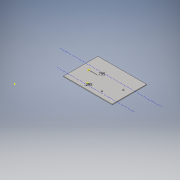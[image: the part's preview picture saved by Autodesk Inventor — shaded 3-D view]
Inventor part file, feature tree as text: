
AUTODESK INVENTOR PART (.ipt)
format: ipt  version: 2016 (Build 200138000, 138)  size: 113,664 bytes
history: native  units: in
note: dims shown in document units (in); Inventor stores cm internally (conversion verified against a paired STEP export)
features: sketch x3, extrude x1, hole x1
ambient origin geometry x8: Origin, YZ Plane, XZ Plane, XY Plane, X Axis, Y Axis, Z Axis, Center Point
bodies: Solid1 (feature_tree)
feature tree (5):
  extrude  "Extrusion1"  Depth=6.0in
  hole  "Hole1"  [1 undecoded]
  sketch  "Sketch5"  dims[d5=1.0236in d7=3.1102in d12=0.2362in d13=0.75in d14=0.375in d15=0.25in d16=0.5635in d17=1.0in d18=0.8108in d19=1.2343in d20=3.1102in d21=1.0236in d22=3.124in d23=7.3366in d45=0.2953in d46=0.7953in]
  sketch  "Sketch1"  dims[d0=8.5in d1=6.0in]
  sketch  "Sketch2"  dims[d2=0.125in d3=0.0in d4=5.6831in]
note: 1 required parameter value undecoded (feature->parameter linkage not recoverable at this tier; creation-order binding heuristic only, values carry confidence <= 0.55)
